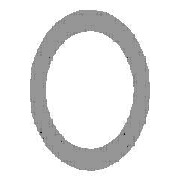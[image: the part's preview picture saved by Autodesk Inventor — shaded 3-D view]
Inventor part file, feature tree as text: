
AUTODESK INVENTOR PART (.ipt)
format: ipt  version: 2013 (Build 170138000, 138)  size: 107,520 bytes
history: native  units: mm (DEFAULTED — no unit token found)
features: other x4, sketch x3, plane x1
ambient origin geometry x8: Origin, YZ Plane, XZ Plane, XY Plane, X Axis, Y Axis, Z Axis, Center Point
bodies: Solid1 (feature_tree), Body (feature_tree)
feature tree (8):
  parser-record x1  (decoder bookkeeping rows leaked as tree rows — omitted from the tree; the rows remain in map.json)
  other  "Driven Length"
  other  "Start plane"
  other  "End plane"
  sketch  "Sketch"  dims[d2=1011.6312mm d3=0.0mm d4=-0.0mm d5=1011.6312mm d6=90.0deg d7=1011.6312mm]
  sketch  "Sketch3"  dims[d0=33.401mm]
  plane  "Work Plane3"
  sketch  "Sketch4"  dims[d1=3.3782mm]
